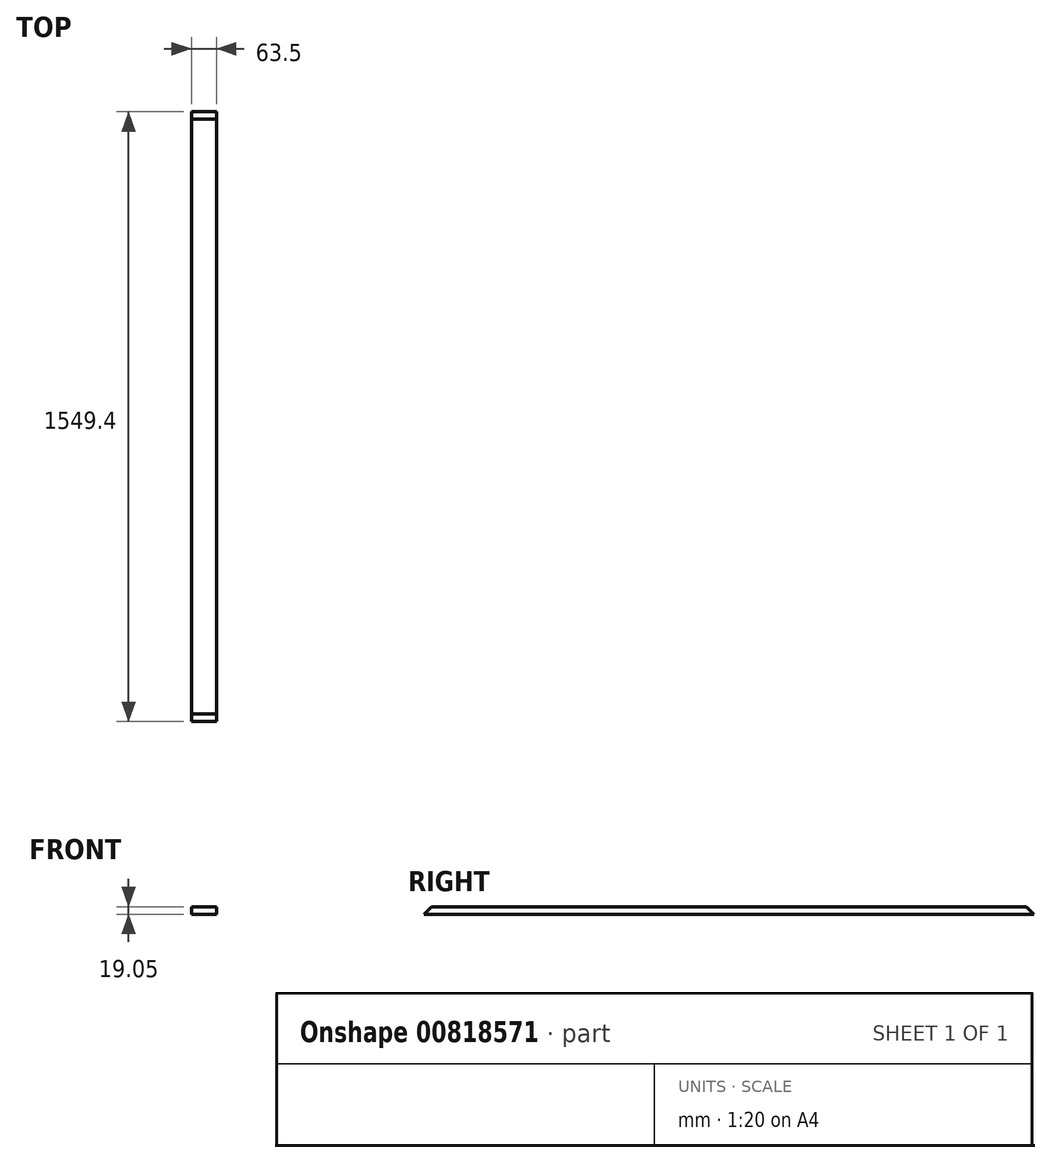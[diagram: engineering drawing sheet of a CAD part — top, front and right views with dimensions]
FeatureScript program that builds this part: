
annotation { "Feature Type Name" : "Feature", "Feature Type Description" : "" }
export const myFeature = defineFeature(function(context is Context, id is Id, definition is map)
    precondition{}
    {
        {
            var Q0;
            Q0=qCreatedBy(makeId("Front.planeOp"),FACE);
            var sketch = newSketch(context, id + "F0", { "sketchPlane" : qUnion([Q0])});
            skLineSegment(sketch, "E0.bottom", {"start": v(-26.64, 23.77) * mm, "end": v(36.86, 23.77) * mm});
            skLineSegment(sketch, "E0.top", {"start": v(-26.64, -14.33) * mm, "end": v(36.86, -14.33) * mm});
            skLineSegment(sketch, "E0.left", {"start": v(-26.64, 23.77) * mm, "end": v(-26.64, -14.33) * mm});
            skLineSegment(sketch, "E0.right", {"start": v(36.86, 23.77) * mm, "end": v(36.86, -14.33) * mm});
            skSolve(sketch);
        }
        {
            var Q0;
            Q0=qSketchRegion(id+"F0",true);
            extrude(context, id + "F1", {"entities" : qUnion([Q0]), "depth" : 1549.4 * mm, "offsetDistance" : 25.4 * mm});
        }
        {
            var Q0;
            Q0=makeQuery(id+"F1.opExtrude","SWEPT_FACE",FACE,{"disambiguationData":[OSD([sQuery(id+"F0.wireOp",EDGE,"E0.right")])]});
            var sketch = newSketch(context, id + "F2", { "sketchPlane" : qUnion([Q0])});
            skLineSegment(sketch, "E1", {"start": v(-1549.4, -14.33) * mm, "end": v(-1549.4, 23.77) * mm});
            skLineSegment(sketch, "E2", {"start": v(-1549.4, 23.77) * mm, "end": v(-1511.3, 23.77) * mm});
            skLineSegment(sketch, "E3", {"start": v(-1511.3, 23.77) * mm, "end": v(-1549.4, -14.33) * mm});
            skLineSegment(sketch, "E4", {"start": v(0, -14.33) * mm, "end": v(-38.1, 23.77) * mm});
            skLineSegment(sketch, "E5", {"start": v(-38.1, 23.77) * mm, "end": v(0, 23.77) * mm});
            skLineSegment(sketch, "E6", {"start": v(0, 23.77) * mm, "end": v(0, -14.33) * mm});
            skSolve(sketch);
        }
        {
            var Q0;
            Q0=qSketchRegion(id+"F2",true);
            extrude(context, id + "F3", {"entities" : qUnion([Q0]), "operationType" : NewBodyOperationType.REMOVE, "oppositeDirection" : true, "depth" : 76.2 * mm, "offsetDistance" : 25.4 * mm});
        }
        {
            var Q0;
            Q0=qCreatedBy(makeId("Front.planeOp"),FACE);
            var sketch = newSketch(context, id + "F4", { "sketchPlane" : qUnion([Q0])});
            skLineSegment(sketch, "E7.bottom", {"start": v(-26.64, 23.77) * mm, "end": v(36.86, 23.77) * mm});
            skLineSegment(sketch, "E7.top", {"start": v(-26.64, 4.72) * mm, "end": v(36.86, 4.72) * mm});
            skLineSegment(sketch, "E7.left", {"start": v(-26.64, 23.77) * mm, "end": v(-26.64, 4.72) * mm});
            skLineSegment(sketch, "E7.right", {"start": v(36.86, 23.77) * mm, "end": v(36.86, 4.72) * mm});
            skSolve(sketch);
        }
        {
            var Q0;
            Q0 = qSketchRegion(id + "F4", true);
            extrude(context, id + "F5", {"entities" : qUnion([Q0]), "operationType" : NewBodyOperationType.REMOVE, "endBound" : BoundingType.THROUGH_ALL, "depth" : 25.4 * mm, "offsetDistance" : 25.4 * mm});
        }
    });
